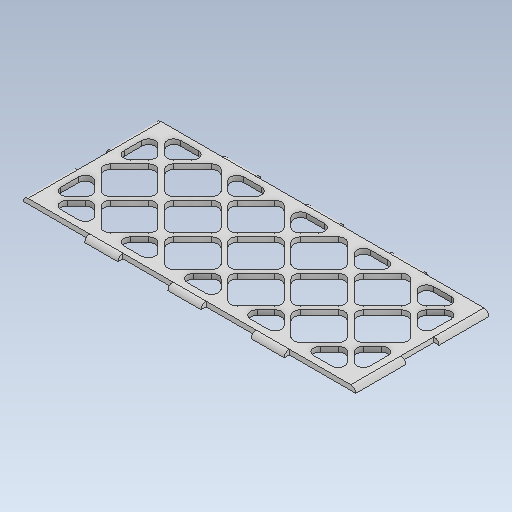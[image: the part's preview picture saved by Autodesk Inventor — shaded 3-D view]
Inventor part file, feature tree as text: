
AUTODESK INVENTOR PART (.ipt)
format: ipt  version: 2020 (Build 240168000, 168)  size: 484,352 bytes
history: native  units: in
note: dims shown in document units (in); Inventor stores cm internally (conversion verified against a paired STEP export)
features: fillet x2, extrude x1, sketch x1
ambient origin geometry x8: Origin, YZ Plane, XZ Plane, XY Plane, X Axis, Y Axis, Z Axis, Center Point
bodies: Solid1 (feature_tree)
feature tree (4):
  extrude  "Extrusion1"  Depth=1.5748in
  fillet  "Fillet1"  Radius=0.9843in
  fillet  "Fillet2"  Radius=0.9843in
  sketch  "Sketch1"  dims[d0=3.937in d1=1.5748in d2=0.9843in d3=0.9843in d4=0.9843in d5=0.9843in d6=0.1969in d7=0.3937in d8=0.0591in d9=0.1969in d10=0.3937in d11=0.0591in d12=0.1969in d13=0.3937in d14=0.0591in d15=0.1969in d16=0.0591in d17=0.3937in d18=0.1969in d19=0.0591in d20=0.3937in d27=0.0984in d28=0.748in d29=0.748in d30=0.748in d31=0.748in d32=0.748in d33=0.0984in d34=0.0394in d35=1.9685in d37=0.748in d38=0.3937in d40=1.0in d42=135.0deg d43=1.5748in d45=0.748in d46=0.3937in d48=1.0in d50=1.9685in d52=0.748in d53=0.3937in d55=1.0in d57=0.3937in d58=0.0591in d59=0.3937in d60=0.0591in d61=0.3937in d62=0.0591in d63=0.0591in d64=0.0in d65=0.0787in d66=0.0591in d44=0.5in]
